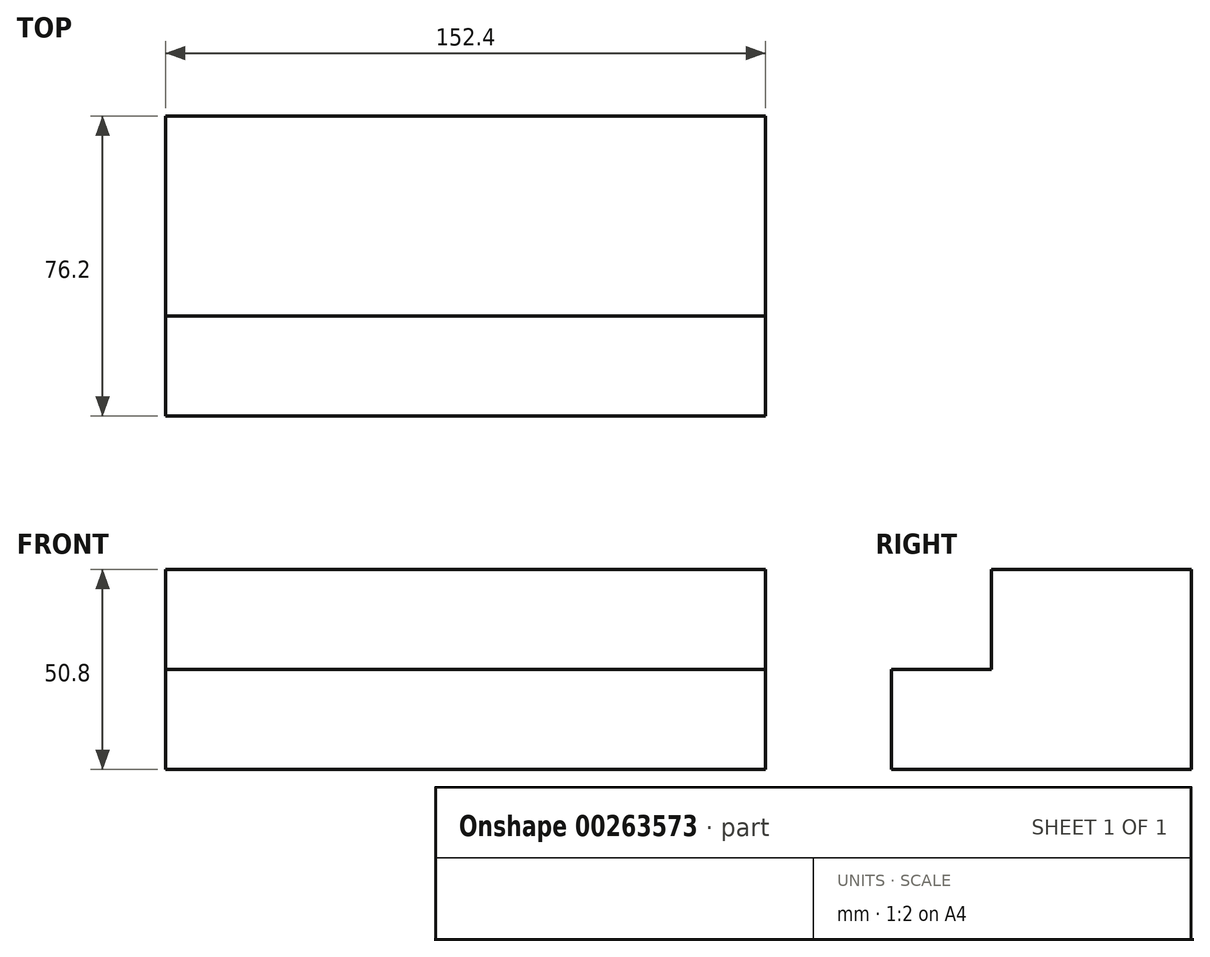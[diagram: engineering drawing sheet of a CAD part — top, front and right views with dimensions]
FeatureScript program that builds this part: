
annotation { "Feature Type Name" : "Feature", "Feature Type Description" : "" }
export const myFeature = defineFeature(function(context is Context, id is Id, definition is map)
    precondition{}
    {
        {
            var Q0;
            Q0=qCreatedBy(makeId("Front.planeOp"),FACE);
            var sketch = newSketch(context, id + "F0", { "sketchPlane" : qUnion([Q0])});
            skLineSegment(sketch, "E0.bottom", {"start": v(-80.95, 22.96) * mm, "end": v(71.45, 22.96) * mm});
            skLineSegment(sketch, "E0.top", {"start": v(-80.95, -27.84) * mm, "end": v(71.45, -27.84) * mm});
            skLineSegment(sketch, "E0.left", {"start": v(-80.95, 22.96) * mm, "end": v(-80.95, -27.84) * mm});
            skLineSegment(sketch, "E0.right", {"start": v(71.45, 22.96) * mm, "end": v(71.45, -27.84) * mm});
            skSolve(sketch);
        }
        {
            var Q0;
            Q0=makeQuery(id+"F0.imprint","IMPRINT",FACE,{"disambiguationData":[TD([[makeQuery(id+"F0.imprint","IMPRINT",EDGE,{"derivedFrom":sQuery(id+"F0.wireOp",EDGE,"E0.bottom")}),-1.0]])]});
            extrude(context, id + "F1", {"entities" : qUnion([Q0]), "depth" : 76.2 * mm});
        }
        {
            var Q0;
            Q0=makeQuery(id+"F1.opExtrude","SWEPT_FACE",FACE,{"disambiguationData":[OSD([sQuery(id+"F0.wireOp",EDGE,"E0.right")])]});
            var sketch = newSketch(context, id + "F2", { "sketchPlane" : qUnion([Q0])});
            skLineSegment(sketch, "E1", {"start": v(-76.2, -2.44) * mm, "end": v(-50.8, -2.44) * mm});
            skLineSegment(sketch, "E2", {"start": v(-50.8, -2.44) * mm, "end": v(-50.8, 22.96) * mm});
            skLineSegment(sketch, "E3", {"start": v(-50.8, 22.96) * mm, "end": v(-76.2, 22.96) * mm});
            skLineSegment(sketch, "E4", {"start": v(-76.2, 22.96) * mm, "end": v(-76.2, -2.44) * mm});
            skSolve(sketch);
        }
        {
            var Q0;
            Q0 = qSketchRegion(id + "F2", true);
            extrude(context, id + "F3", {"entities" : qUnion([Q0]), "operationType" : NewBodyOperationType.REMOVE, "endBound" : BoundingType.THROUGH_ALL, "oppositeDirection" : true, "depth" : 25.4 * mm});
        }
    });
